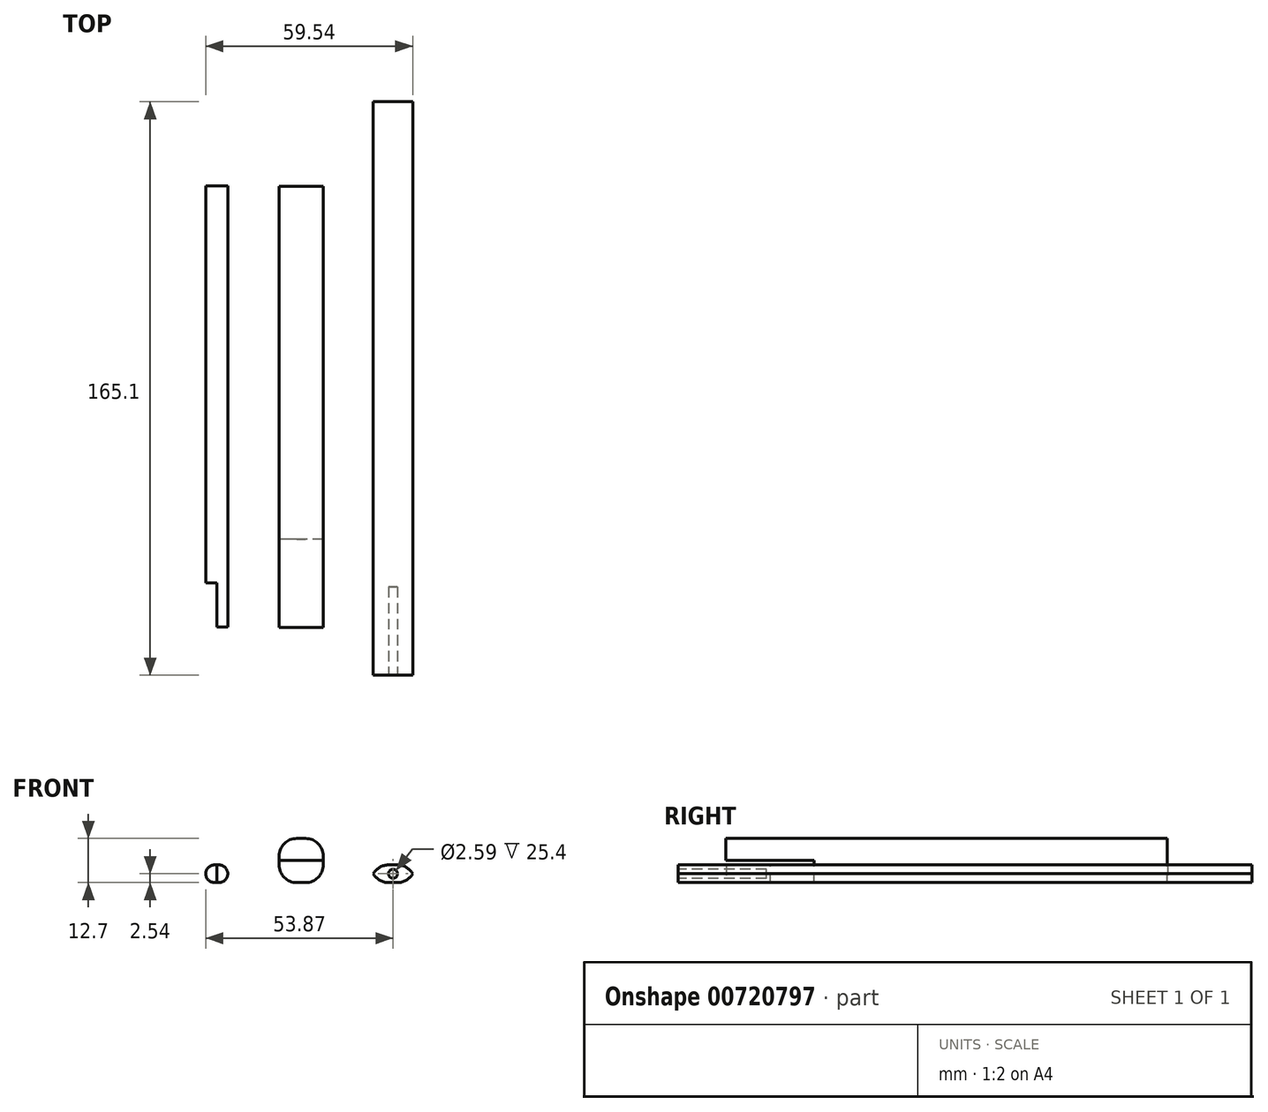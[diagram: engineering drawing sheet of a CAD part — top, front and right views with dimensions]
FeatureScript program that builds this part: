
annotation { "Feature Type Name" : "Feature", "Feature Type Description" : "" }
export const myFeature = defineFeature(function(context is Context, id is Id, definition is map)
    precondition{}
    {
        {
            var Q0;
            Q0=qCreatedBy(makeId("Top.planeOp"),FACE);
            var sketch = newSketch(context, id + "F0", { "sketchPlane" : qUnion([Q0])});
            skLineSegment(sketch, "E0.bottom", {"start": v(-47.52, 71.2) * mm, "end": v(-41.17, 71.2) * mm});
            skLineSegment(sketch, "E0.top", {"start": v(-47.52, -55.8) * mm, "end": v(-41.17, -55.8) * mm});
            skLineSegment(sketch, "E0.left", {"start": v(-47.52, 71.2) * mm, "end": v(-47.52, -55.8) * mm});
            skLineSegment(sketch, "E0.right", {"start": v(-41.17, 71.2) * mm, "end": v(-41.17, -55.8) * mm});
            skSolve(sketch);
        }
        {
            var Q0;
            Q0=makeQuery(id+"F0.imprint","IMPRINT",FACE,{"disambiguationData":[TD([[makeQuery(id+"F0.imprint","IMPRINT",EDGE,{"derivedFrom":sQuery(id+"F0.wireOp",EDGE,"E0.bottom")}),-1.0]])]});
            extrude(context, id + "F1", {"entities" : qUnion([Q0]), "depth" : 5.08 * mm, "offsetDistance" : 25.4 * mm});
        }
        {
            var Q0;
            Q0=makeQuery(id+"F1.opExtrude","CAP_EDGE",EDGE,{"disambiguationData":[OSD([sQuery(id+"F0.wireOp",EDGE,"E0.left")])],"isStart":false});
            var Q1;
            Q1=makeQuery(id+"F1.opExtrude","CAP_EDGE",EDGE,{"disambiguationData":[OSD([sQuery(id+"F0.wireOp",EDGE,"E0.right")])],"isStart":false});
            var Q2;
            Q2=makeQuery(id+"F1.opExtrude","CAP_EDGE",EDGE,{"disambiguationData":[OSD([sQuery(id+"F0.wireOp",EDGE,"E0.right")])],"isStart":true});
            var Q3;
            Q3=makeQuery(id+"F1.opExtrude","CAP_EDGE",EDGE,{"disambiguationData":[OSD([sQuery(id+"F0.wireOp",EDGE,"E0.left")])],"isStart":true});
            fillet(context, id + "F2", {"entities" : qUnion([Q0, Q1, Q2, Q3]), "radius" : 2.54 * mm, "tangentPropagation" : true, "allowEdgeOverflow" : false});
        }
        {
            var Q0;
            Q0=makeQuery(id+"F1.opExtrude","SWEPT_FACE",FACE,{"disambiguationData":[OSD([sQuery(id+"F0.wireOp",EDGE,"E0.top")])]});
            var sketch = newSketch(context, id + "F3", { "sketchPlane" : qUnion([Q0])});
            skLineSegment(sketch, "E1", {"start": v(-39.41, 2.54) * mm, "end": v(-53.16, 2.54) * mm});
            skPoint(sketch, "E1.startSnap0", {"position": v(-41.17, 2.54) * mm});
            skPoint(sketch, "E1.endSnap0", {"position": v(-47.52, 2.54) * mm});
            skLineSegment(sketch, "E2", {"start": v(-44.34, 5.08) * mm, "end": v(-44.34, 0) * mm});
            skCircle(sketch, "E3", {"center": v(-44.34, 2.54) * mm, "radius": 0.77 * mm});
            skSolve(sketch);
        }
        {
            var Q0;
            {var subQ0=sQuery(id+"F3.wireOp",EDGE,"E2");var subQ1=sQuery(id+"F3.wireOp",EDGE,"E1");var subQ2=makeQuery(id+"F3.imprint","INTERSECT",VERTEX,{"derivedFrom":[subQ1,subQ0]});Q0=makeQuery(id+"F3.imprint","IMPRINT",FACE,{"disambiguationData":[TD([[makeQuery(id+"F3.imprint","IMPRINT",EDGE,{"disambiguationData":[TD([[subQ2,-1.0]])],"derivedFrom":subQ1}),-1.0]])]});}
            var Q1;
            {var subQ0=sQuery(id+"F3.wireOp",EDGE,"E3");var subQ1=sQuery(id+"F3.wireOp",EDGE,"E1");var subQ2=makeQuery(id+"F3.imprint","INTERSECT",VERTEX,{"disambiguationData":[OD(0.0)],"derivedFrom":[subQ1,subQ0]});Q1=makeQuery(id+"F3.imprint","IMPRINT",FACE,{"disambiguationData":[TD([[makeQuery(id+"F3.imprint","IMPRINT",EDGE,{"disambiguationData":[TD([[subQ2,-1.0]])],"derivedFrom":subQ1}),-1.0]])]});}
            var Q2;
            {var subQ0=sQuery(id+"F3.wireOp",EDGE,"E3");var subQ1=sQuery(id+"F3.wireOp",EDGE,"E1");var subQ2=makeQuery(id+"F3.imprint","INTERSECT",VERTEX,{"disambiguationData":[OD(0.0)],"derivedFrom":[subQ1,subQ0]});Q2=makeQuery(id+"F3.imprint","IMPRINT",FACE,{"disambiguationData":[TD([[makeQuery(id+"F3.imprint","IMPRINT",EDGE,{"disambiguationData":[TD([[subQ2,-1.0]])],"derivedFrom":subQ1}),1.0]])]});}
            var Q3;
            {var subQ0=sQuery(id+"F3.wireOp",EDGE,"E2");var subQ1=sQuery(id+"F3.wireOp",EDGE,"E1");var subQ2=makeQuery(id+"F3.imprint","INTERSECT",VERTEX,{"derivedFrom":[subQ1,subQ0]});Q3=makeQuery(id+"F3.imprint","IMPRINT",FACE,{"disambiguationData":[TD([[makeQuery(id+"F3.imprint","IMPRINT",EDGE,{"disambiguationData":[TD([[subQ2,-1.0]])],"derivedFrom":subQ1}),1.0]])]});}
            var Q4;
            Q4=sQuery(id+"F3.wireOp",EDGE,"E3");
            extrude(context, id + "F4", {"entities" : qUnion([Q0, Q1, Q2, Q3]), "operationType" : NewBodyOperationType.REMOVE, "surfaceEntities" : qUnion([Q4]), "oppositeDirection" : true, "depth" : 12.7 * mm, "offsetDistance" : 25.4 * mm});
        }
        {
            var Q0;
            Q0=qCreatedBy(makeId("Top.planeOp"),FACE);
            var sketch = newSketch(context, id + "F5", { "sketchPlane" : qUnion([Q0])});
            skLineSegment(sketch, "E4.bottom", {"start": v(-26.42, 71.1) * mm, "end": v(-13.72, 71.1) * mm});
            skLineSegment(sketch, "E4.top", {"start": v(-26.42, -55.9) * mm, "end": v(-13.72, -55.9) * mm});
            skLineSegment(sketch, "E4.left", {"start": v(-26.42, 71.1) * mm, "end": v(-26.42, -55.9) * mm});
            skLineSegment(sketch, "E4.right", {"start": v(-13.72, 71.1) * mm, "end": v(-13.72, -55.9) * mm});
            skSolve(sketch);
        }
        {
            var Q0;
            Q0=makeQuery(id+"F5.imprint","IMPRINT",FACE,{"disambiguationData":[TD([[makeQuery(id+"F5.imprint","IMPRINT",EDGE,{"derivedFrom":sQuery(id+"F5.wireOp",EDGE,"E4.bottom")}),-1.0]])]});
            extrude(context, id + "F6", {"entities" : qUnion([Q0]), "depth" : 12.7 * mm, "offsetDistance" : 25.4 * mm});
        }
        {
            var Q0;
            Q0=makeQuery(id+"F6.opExtrude","CAP_EDGE",EDGE,{"disambiguationData":[OSD([sQuery(id+"F5.wireOp",EDGE,"E4.left")])],"isStart":false});
            var Q1;
            Q1=makeQuery(id+"F6.opExtrude","CAP_EDGE",EDGE,{"disambiguationData":[OSD([sQuery(id+"F5.wireOp",EDGE,"E4.right")])],"isStart":false});
            var Q2;
            Q2=makeQuery(id+"F6.opExtrude","CAP_EDGE",EDGE,{"disambiguationData":[OSD([sQuery(id+"F5.wireOp",EDGE,"E4.right")])],"isStart":true});
            var Q3;
            Q3=makeQuery(id+"F6.opExtrude","CAP_EDGE",EDGE,{"disambiguationData":[OSD([sQuery(id+"F5.wireOp",EDGE,"E4.left")])],"isStart":true});
            fillet(context, id + "F7", {"entities" : qUnion([Q0, Q1, Q2, Q3]), "radius" : 5.08 * mm, "tangentPropagation" : true, "allowEdgeOverflow" : false});
        }
        {
            var Q0;
            Q0=makeQuery(id+"F6.opExtrude","SWEPT_FACE",FACE,{"disambiguationData":[OSD([sQuery(id+"F5.wireOp",EDGE,"E4.top")])]});
            var sketch = newSketch(context, id + "F8", { "sketchPlane" : qUnion([Q0])});
            skLineSegment(sketch, "E5", {"start": v(-20.07, 12.7) * mm, "end": v(-20.07, 0) * mm});
            skLineSegment(sketch, "E6", {"start": v(-13.72, 6.35) * mm, "end": v(-26.42, 6.35) * mm});
            skCircle(sketch, "E7", {"center": v(-20.07, 6.35) * mm, "radius": 2.54 * mm});
            skSolve(sketch);
        }
        {
            var Q0;
            {var subQ0=sQuery(id+"F8.wireOp",EDGE,"E7");var subQ1=sQuery(id+"F8.wireOp",EDGE,"E5");var subQ2=makeQuery(id+"F8.imprint","INTERSECT",VERTEX,{"disambiguationData":[OD(0.0)],"derivedFrom":[subQ1,subQ0]});Q0=makeQuery(id+"F8.imprint","IMPRINT",FACE,{"disambiguationData":[TD([[makeQuery(id+"F8.imprint","IMPRINT",EDGE,{"disambiguationData":[TD([[subQ2,-1.0]])],"derivedFrom":subQ1}),1.0]])]});}
            var Q1;
            {var subQ0=sQuery(id+"F8.wireOp",EDGE,"E7");var subQ1=sQuery(id+"F8.wireOp",EDGE,"E5");var subQ2=makeQuery(id+"F8.imprint","INTERSECT",VERTEX,{"disambiguationData":[OD(0.0)],"derivedFrom":[subQ1,subQ0]});Q1=makeQuery(id+"F8.imprint","IMPRINT",FACE,{"disambiguationData":[TD([[makeQuery(id+"F8.imprint","IMPRINT",EDGE,{"disambiguationData":[TD([[subQ2,-1.0]])],"derivedFrom":subQ1}),-1.0]])]});}
            var Q2;
            {var subQ0=sQuery(id+"F8.wireOp",EDGE,"E6");var subQ1=sQuery(id+"F8.wireOp",EDGE,"E5");var subQ2=makeQuery(id+"F8.imprint","INTERSECT",VERTEX,{"derivedFrom":[subQ1,subQ0]});Q2=makeQuery(id+"F8.imprint","IMPRINT",FACE,{"disambiguationData":[TD([[makeQuery(id+"F8.imprint","IMPRINT",EDGE,{"disambiguationData":[TD([[subQ2,-1.0]])],"derivedFrom":subQ1}),-1.0]])]});}
            var Q3;
            {var subQ0=sQuery(id+"F8.wireOp",EDGE,"E6");var subQ1=sQuery(id+"F8.wireOp",EDGE,"E5");var subQ2=makeQuery(id+"F8.imprint","INTERSECT",VERTEX,{"derivedFrom":[subQ1,subQ0]});Q3=makeQuery(id+"F8.imprint","IMPRINT",FACE,{"disambiguationData":[TD([[makeQuery(id+"F8.imprint","IMPRINT",EDGE,{"disambiguationData":[TD([[subQ2,-1.0]])],"derivedFrom":subQ1}),1.0]])]});}
            var Q4;
            Q4=sQuery(id+"F8.wireOp",EDGE,"E7");
            extrude(context, id + "F9", {"entities" : qUnion([Q0, Q1, Q2, Q3]), "operationType" : NewBodyOperationType.REMOVE, "surfaceEntities" : qUnion([Q4]), "oppositeDirection" : true, "depth" : 25.4 * mm, "offsetDistance" : 25.4 * mm});
        }
        {
            var Q0;
            Q0=qCreatedBy(makeId("Top.planeOp"),FACE);
            var sketch = newSketch(context, id + "F10", { "sketchPlane" : qUnion([Q0])});
            skLineSegment(sketch, "E8", {"start": v(0, -69.66) * mm, "end": v(0, 95.44) * mm});
            skLineSegment(sketch, "E9", {"start": v(0, -69.66) * mm, "end": v(12.7, -69.66) * mm});
            skLineSegment(sketch, "E10", {"start": v(12.7, -69.66) * mm, "end": v(12.7, 95.44) * mm});
            skLineSegment(sketch, "E11", {"start": v(0, 95.44) * mm, "end": v(12.7, 95.44) * mm});
            skSolve(sketch);
        }
        {
            var Q0;
            Q0=makeQuery(id+"F10.imprint","IMPRINT",FACE,{"disambiguationData":[TD([[makeQuery(id+"F10.imprint","IMPRINT",EDGE,{"derivedFrom":sQuery(id+"F10.wireOp",EDGE,"E8")}),-1.0]])]});
            extrude(context, id + "F11", {"entities" : qUnion([Q0]), "depth" : 5.08 * mm, "offsetDistance" : 25.4 * mm});
        }
        {
            var Q0;
            Q0=makeQuery(id+"F11.opExtrude","CAP_EDGE",EDGE,{"disambiguationData":[OSD([sQuery(id+"F10.wireOp",EDGE,"E10")])],"isStart":false});
            var Q1;
            Q1=makeQuery(id+"F11.opExtrude","CAP_EDGE",EDGE,{"disambiguationData":[OSD([sQuery(id+"F10.wireOp",EDGE,"E8")])],"isStart":false});
            var Q2;
            Q2=makeQuery(id+"F11.opExtrude","CAP_EDGE",EDGE,{"disambiguationData":[OSD([sQuery(id+"F10.wireOp",EDGE,"E10")])],"isStart":true});
            var Q3;
            Q3=makeQuery(id+"F11.opExtrude","CAP_EDGE",EDGE,{"disambiguationData":[OSD([sQuery(id+"F10.wireOp",EDGE,"E8")])],"isStart":true});
            fillet(context, id + "F12", {"entities" : qUnion([Q0, Q1, Q2, Q3]), "radius" : 5.08 * mm, "tangentPropagation" : true, "allowEdgeOverflow" : false});
        }
        {
            var Q0;
            Q0=makeQuery(id+"F11.opExtrude","SWEPT_FACE",FACE,{"disambiguationData":[OSD([sQuery(id+"F10.wireOp",EDGE,"E9")])]});
            var sketch = newSketch(context, id + "F13", { "sketchPlane" : qUnion([Q0])});
            skLineSegment(sketch, "E12", {"start": v(6.35, 5.08) * mm, "end": v(6.35, 0) * mm});
            skLineSegment(sketch, "E13", {"start": v(0.68, 2.54) * mm, "end": v(12.02, 2.54) * mm});
            skCircle(sketch, "E14", {"center": v(6.35, 2.54) * mm, "radius": 1.3 * mm});
            skSolve(sketch);
        }
        {
            var Q0;
            {var subQ0=sQuery(id+"F13.wireOp",EDGE,"E14");var subQ1=sQuery(id+"F13.wireOp",EDGE,"E12");var subQ2=makeQuery(id+"F13.imprint","INTERSECT",VERTEX,{"disambiguationData":[OD(0.0)],"derivedFrom":[subQ1,subQ0]});Q0=makeQuery(id+"F13.imprint","IMPRINT",FACE,{"disambiguationData":[TD([[makeQuery(id+"F13.imprint","IMPRINT",EDGE,{"disambiguationData":[TD([[subQ2,-1.0]])],"derivedFrom":subQ1}),1.0]])]});}
            var Q1;
            {var subQ0=sQuery(id+"F13.wireOp",EDGE,"E14");var subQ1=sQuery(id+"F13.wireOp",EDGE,"E12");var subQ2=makeQuery(id+"F13.imprint","INTERSECT",VERTEX,{"disambiguationData":[OD(0.0)],"derivedFrom":[subQ1,subQ0]});Q1=makeQuery(id+"F13.imprint","IMPRINT",FACE,{"disambiguationData":[TD([[makeQuery(id+"F13.imprint","IMPRINT",EDGE,{"disambiguationData":[TD([[subQ2,-1.0]])],"derivedFrom":subQ1}),-1.0]])]});}
            var Q2;
            {var subQ0=sQuery(id+"F13.wireOp",EDGE,"E13");var subQ1=sQuery(id+"F13.wireOp",EDGE,"E12");var subQ2=makeQuery(id+"F13.imprint","INTERSECT",VERTEX,{"derivedFrom":[subQ1,subQ0]});Q2=makeQuery(id+"F13.imprint","IMPRINT",FACE,{"disambiguationData":[TD([[makeQuery(id+"F13.imprint","IMPRINT",EDGE,{"disambiguationData":[TD([[subQ2,-1.0]])],"derivedFrom":subQ1}),-1.0]])]});}
            var Q3;
            {var subQ0=sQuery(id+"F13.wireOp",EDGE,"E13");var subQ1=sQuery(id+"F13.wireOp",EDGE,"E12");var subQ2=makeQuery(id+"F13.imprint","INTERSECT",VERTEX,{"derivedFrom":[subQ1,subQ0]});Q3=makeQuery(id+"F13.imprint","IMPRINT",FACE,{"disambiguationData":[TD([[makeQuery(id+"F13.imprint","IMPRINT",EDGE,{"disambiguationData":[TD([[subQ2,-1.0]])],"derivedFrom":subQ1}),1.0]])]});}
            extrude(context, id + "F14", {"entities" : qUnion([Q0, Q1, Q2, Q3]), "operationType" : NewBodyOperationType.REMOVE, "oppositeDirection" : true, "depth" : 25.4 * mm, "offsetDistance" : 25.4 * mm});
        }
    });
